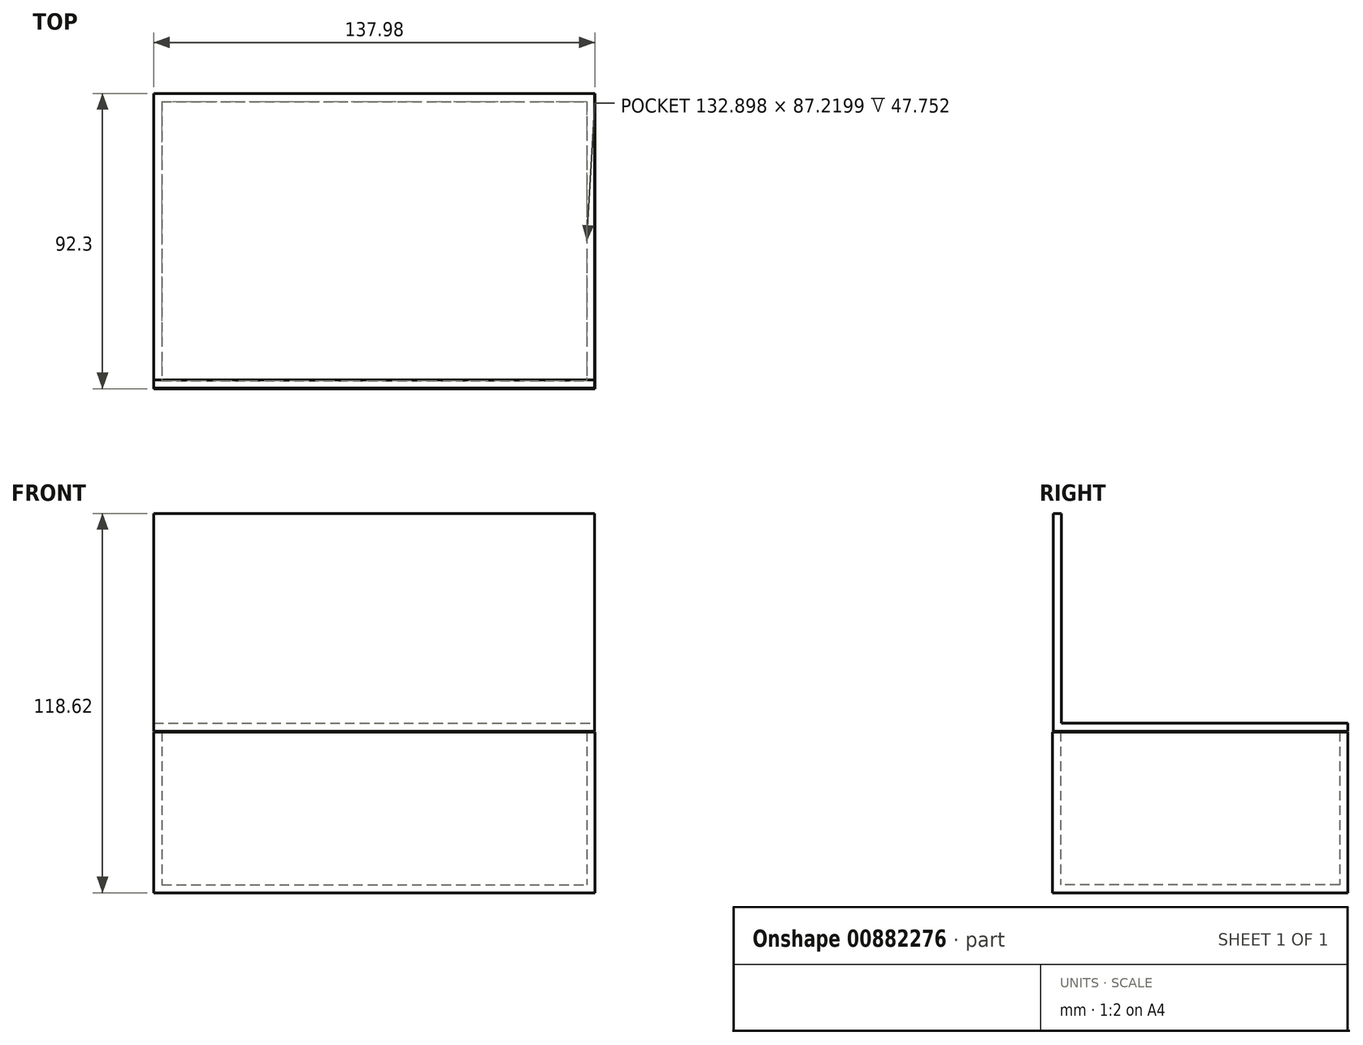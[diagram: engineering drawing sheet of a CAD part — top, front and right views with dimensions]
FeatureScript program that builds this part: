
annotation { "Feature Type Name" : "Feature", "Feature Type Description" : "" }
export const myFeature = defineFeature(function(context is Context, id is Id, definition is map)
    precondition{}
    {
        {
            var Q0;
            Q0=qCreatedBy(makeId("Top.planeOp"),FACE);
            var sketch = newSketch(context, id + "F0", { "sketchPlane" : qUnion([Q0])});
            skLineSegment(sketch, "E0.bottom", {"start": v(-69.5, 52.18) * mm, "end": v(68.48, 52.18) * mm});
            skLineSegment(sketch, "E0.top", {"start": v(-69.5, -40.12) * mm, "end": v(68.48, -40.12) * mm});
            skLineSegment(sketch, "E0.left", {"start": v(-69.5, 52.18) * mm, "end": v(-69.5, -40.12) * mm});
            skLineSegment(sketch, "E0.right", {"start": v(68.48, 52.18) * mm, "end": v(68.48, -40.12) * mm});
            skSolve(sketch);
        }
        {
            var Q0;
            Q0 = qSketchRegion(id + "F0", true);
            extrude(context, id + "F1", {"entities" : qUnion([Q0]), "depth" : 3.3 * mm, "offsetDistance" : 25.4 * mm});
        }
        {
            var Q0;
            Q0=makeQuery(id+"F1.opExtrude","CAP_FACE",FACE,{"disambiguationData":[OSD([sQuery(id+"F0.wireOp",EDGE,"E0.bottom"),sQuery(id+"F0.wireOp",EDGE,"E0.top"),sQuery(id+"F0.wireOp",EDGE,"E0.left"),sQuery(id+"F0.wireOp",EDGE,"E0.right")])],"isStart":false});
            extrude(context, id + "F2", {"entities" : qUnion([Q0]), "operationType" : NewBodyOperationType.ADD, "depth" : 47 * mm, "offsetDistance" : 25.4 * mm});
        }
        {
            var Q0;
            Q0=makeQuery(id+"F2.opExtrude","CAP_FACE",FACE,{"disambiguationData":[OSD([sQuery(id+"F0.wireOp",EDGE,"E0.bottom"),sQuery(id+"F0.wireOp",EDGE,"E0.top"),sQuery(id+"F0.wireOp",EDGE,"E0.left"),sQuery(id+"F0.wireOp",EDGE,"E0.right")])],"isStart":false});
            shell(context, id + "F3", {"entities" : qUnion([Q0]), "thickness" : 2.54 * mm});
        }
        {
            var Q0;
            Q0=qCreatedBy(makeId("Top.planeOp"),FACE);
            cPlane(context, id + "F4", {"entities" : qUnion([Q0]), "cplaneType" : CPlaneType.OFFSET, "offset" : 50.55 * mm, "width" : 152.4 * mm, "height" : 152.4 * mm});
        }
        {
            var Q0;
            Q0=qCreatedBy(id+"F4.planeOp",FACE);
            var sketch = newSketch(context, id + "F5", { "sketchPlane" : qUnion([Q0])});
            skLineSegment(sketch, "E1.bottom", {"start": v(-69.5, -39.93) * mm, "end": v(68.29, -39.93) * mm});
            skLineSegment(sketch, "E1.top", {"start": v(-69.5, 52.18) * mm, "end": v(68.29, 52.18) * mm});
            skLineSegment(sketch, "E1.left", {"start": v(-69.5, -39.93) * mm, "end": v(-69.5, 52.18) * mm});
            skLineSegment(sketch, "E1.right", {"start": v(68.29, -39.93) * mm, "end": v(68.29, 52.18) * mm});
            skSolve(sketch);
        }
        {
            var Q0;
            Q0 = qSketchRegion(id + "F5", true);
            extrude(context, id + "F6", {"entities" : qUnion([Q0]), "depth" : 68.07 * mm, "offsetDistance" : 25.4 * mm});
        }
        {
            var Q0;
            Q0=makeQuery(id+"F6.opExtrude","SWEPT_FACE",FACE,{"disambiguationData":[OSD([sQuery(id+"F5.wireOp",EDGE,"E1.left")])]});
            var Q1;
            Q1=makeQuery(id+"F6.opExtrude","CAP_FACE",FACE,{"disambiguationData":[OSD([sQuery(id+"F5.wireOp",EDGE,"E1.bottom"),sQuery(id+"F5.wireOp",EDGE,"E1.top"),sQuery(id+"F5.wireOp",EDGE,"E1.left"),sQuery(id+"F5.wireOp",EDGE,"E1.right")])],"isStart":false});
            var Q2;
            Q2=makeQuery(id+"F6.opExtrude","SWEPT_FACE",FACE,{"disambiguationData":[OSD([sQuery(id+"F5.wireOp",EDGE,"E1.right")])]});
            var Q3;
            Q3=makeQuery(id+"F6.opExtrude","SWEPT_FACE",FACE,{"disambiguationData":[OSD([sQuery(id+"F5.wireOp",EDGE,"E1.top")])]});
            shell(context, id + "F7", {"entities" : qUnion([Q0, Q1, Q2, Q3]), "thickness" : 2.54 * mm});
        }
    });
